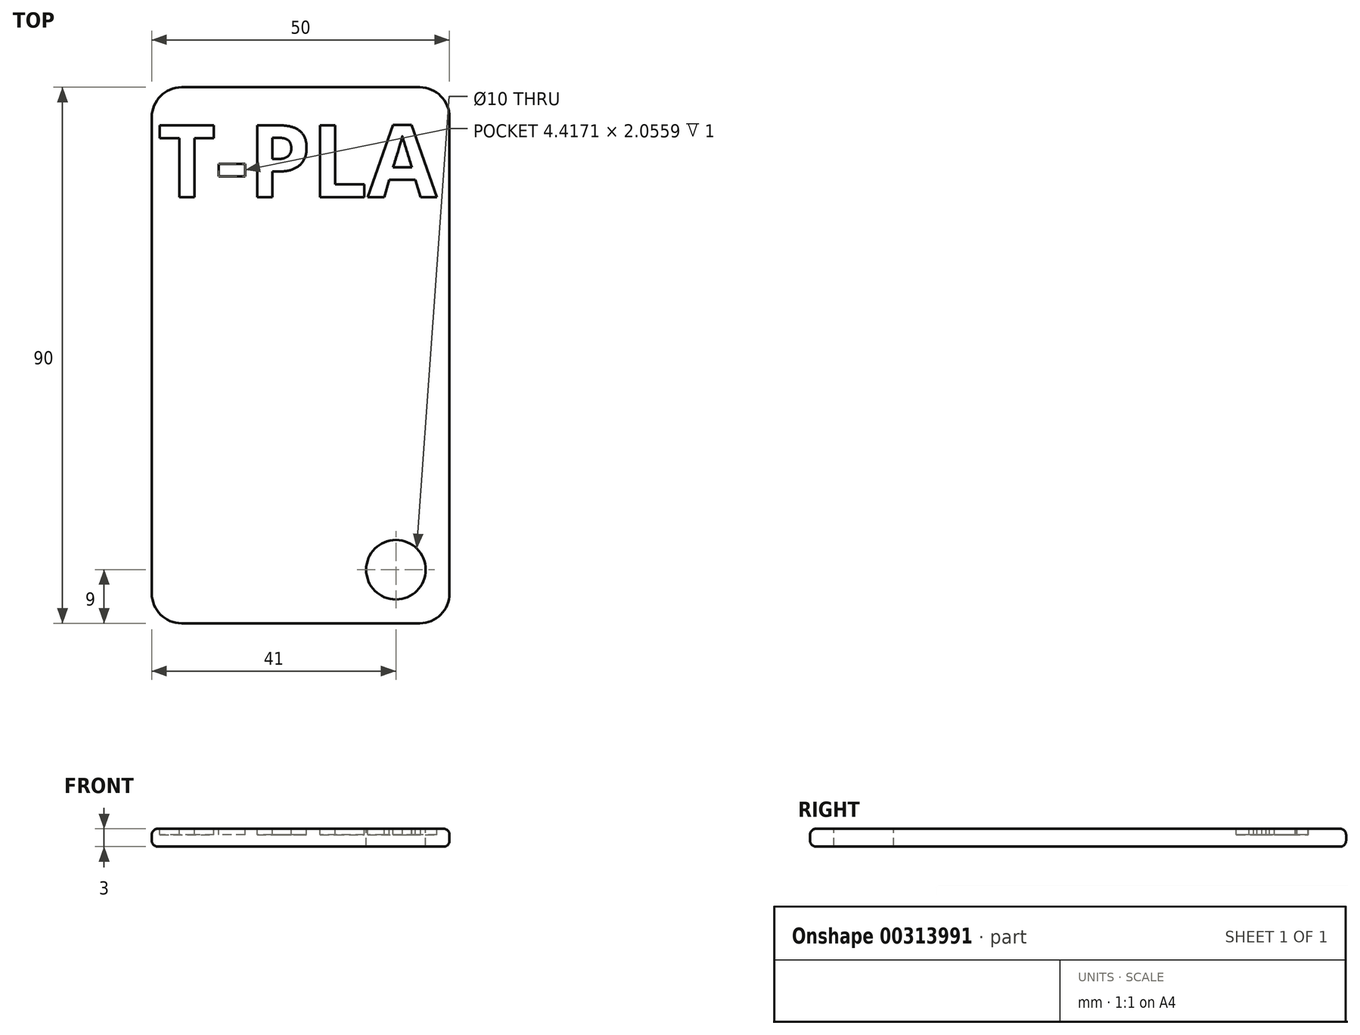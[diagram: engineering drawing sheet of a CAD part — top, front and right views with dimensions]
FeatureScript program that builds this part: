
annotation { "Feature Type Name" : "Feature", "Feature Type Description" : "" }
export const myFeature = defineFeature(function(context is Context, id is Id, definition is map)
    precondition{}
    {
        {
            var Q0;
            Q0=qCreatedBy(makeId("Top.planeOp"),FACE);
            var sketch = newSketch(context, id + "F0", { "sketchPlane" : qUnion([Q0])});
            skLineSegment(sketch, "E0.bottom", {"start": v(-45, 25) * mm, "end": v(45, 25) * mm});
            skLineSegment(sketch, "E0.top", {"start": v(-45, -25) * mm, "end": v(45, -25) * mm});
            skLineSegment(sketch, "E0.left", {"start": v(-45, 25) * mm, "end": v(-45, -25) * mm});
            skLineSegment(sketch, "E0.right", {"start": v(45, 25) * mm, "end": v(45, -25) * mm});
            skLineSegment(sketch, "E1", {"start": v(-45, 25) * mm, "end": v(45, -25) * mm, "construction": true});
            skSolve(sketch);
        }
        {
            var Q0;
            Q0=makeQuery(id+"F0.imprint","IMPRINT",FACE,{"disambiguationData":[TD([[makeQuery(id+"F0.imprint","IMPRINT",EDGE,{"derivedFrom":sQuery(id+"F0.wireOp",EDGE,"E0.bottom")}),-1.0]])]});
            extrude(context, id + "F1", {"entities" : qUnion([Q0]), "depth" : 3 * mm});
        }
        {
            var Q0;
            Q0=makeQuery(id+"F1.opExtrude","CAP_FACE",FACE,{"disambiguationData":[OSD([sQuery(id+"F0.wireOp",EDGE,"E0.bottom"),sQuery(id+"F0.wireOp",EDGE,"E0.top"),sQuery(id+"F0.wireOp",EDGE,"E0.left"),sQuery(id+"F0.wireOp",EDGE,"E0.right")])],"isStart":false});
            var Q1;
            Q1=makeQuery(id+"F1.opExtrude","CAP_FACE",FACE,{"disambiguationData":[OSD([sQuery(id+"F0.wireOp",EDGE,"E0.bottom"),sQuery(id+"F0.wireOp",EDGE,"E0.top"),sQuery(id+"F0.wireOp",EDGE,"E0.left"),sQuery(id+"F0.wireOp",EDGE,"E0.right")])],"isStart":true});
            fillet(context, id + "F2", {"entities" : qUnion([Q0, Q1]), "radius" : 1 * mm, "tangentPropagation" : true, "allowEdgeOverflow" : false});
        }
        {
            var Q0;
            Q0=makeQuery(id+"F1.opExtrude","SWEPT_EDGE",EDGE,{"disambiguationData":[OSD([sQuery(id+"F0.wireOp",EDGE,"E0.top"),sQuery(id+"F0.wireOp",EDGE,"E0.right")])]});
            var Q1;
            Q1=makeQuery(id+"F1.opExtrude","SWEPT_EDGE",EDGE,{"disambiguationData":[OSD([sQuery(id+"F0.wireOp",EDGE,"E0.bottom"),sQuery(id+"F0.wireOp",EDGE,"E0.right")])]});
            var Q2;
            Q2=makeQuery(id+"F1.opExtrude","SWEPT_EDGE",EDGE,{"disambiguationData":[OSD([sQuery(id+"F0.wireOp",EDGE,"E0.bottom"),sQuery(id+"F0.wireOp",EDGE,"E0.left")])]});
            var Q3;
            Q3=makeQuery(id+"F1.opExtrude","SWEPT_EDGE",EDGE,{"disambiguationData":[OSD([sQuery(id+"F0.wireOp",EDGE,"E0.top"),sQuery(id+"F0.wireOp",EDGE,"E0.left")])]});
            fillet(context, id + "F3", {"entities" : qUnion([Q0, Q1, Q2, Q3]), "radius" : 5 * mm, "tangentPropagation" : true, "allowEdgeOverflow" : false});
        }
        {
            var Q0;
            Q0=qCreatedBy(makeId("Right.planeOp"),FACE);
            var sketch = newSketch(context, id + "F4", { "sketchPlane" : qUnion([Q0])});
            skLineSegment(sketch, "E2", {"start": v(0, 0) * mm, "end": v(0, 32.9) * mm});
            skSolve(sketch);
        }
        {
            var Q0;
            Q0=makeQuery(id+"F1.opExtrude","SWEPT_BODY",BODY,{"disambiguationData":[OSD([sQuery(id+"F0.wireOp",EDGE,"E0.bottom"),sQuery(id+"F0.wireOp",EDGE,"E0.top"),sQuery(id+"F0.wireOp",EDGE,"E0.left"),sQuery(id+"F0.wireOp",EDGE,"E0.right")])]});
            var Q1;
            Q1=sQuery(id+"F4.wireOp",EDGE,"E2");
            transform(context, id + "F5", {"entities" : qUnion([Q0]), "transformType" : TransformType.ROTATION, "transformAxis" : qUnion([Q1]), "angle" : 90 * degree, "makeCopy" : false});
        }
        {
            var Q0;
            Q0=makeQuery(id+"F1.opExtrude","CAP_FACE",FACE,{"disambiguationData":[OSD([sQuery(id+"F0.wireOp",EDGE,"E0.bottom"),sQuery(id+"F0.wireOp",EDGE,"E0.top"),sQuery(id+"F0.wireOp",EDGE,"E0.left"),sQuery(id+"F0.wireOp",EDGE,"E0.right")])],"isStart":false});
            var sketch = newSketch(context, id + "F6", { "sketchPlane" : qUnion([Q0])});
            skText(sketch, "E3", { "text": "T-PLA", "fontName": "OpenSans-Bold.ttf"});
            const initialGuessF6  = {"E3": [-0.024, 0.02658, 1, 0, 0.01213]};
            skSetInitialGuess(sketch, initialGuessF6);
            skSolve(sketch);
        }
        {
            var Q0;
            Q0=qSketchRegion(id+"F6",true);
            extrude(context, id + "F7", {"entities" : qUnion([Q0]), "operationType" : NewBodyOperationType.REMOVE, "oppositeDirection" : true, "depth" : 1 * mm});
        }
        {
            var Q0;
            {var subQ0=sQuery(id+"F0.wireOp",EDGE,"E0.left");var subQ2=sQuery(id+"F0.wireOp",EDGE,"E0.bottom");var subQ4=sQuery(id+"F0.wireOp",EDGE,"E0.right");var subQ6=sQuery(id+"F0.wireOp",EDGE,"E0.top");Q0=makeQuery(id+"F7.boolean.opBoolean","SPLIT",FACE,{"disambiguationData":[TD([makeQuery(id+"F7.opExtrude","SWEPT_FACE",FACE,{"disambiguationData":[OSD([sQuery(id+"F6.wireOp",EDGE,"E3.sketch_text.stroke-0")])]})])],"derivedFrom":makeQuery(id+"F1.opExtrude","CAP_FACE",FACE,{"disambiguationData":[OSD([subQ2,subQ6,subQ0,subQ4])],"isStart":false})});}
            var sketch = newSketch(context, id + "F8", { "sketchPlane" : qUnion([Q0])});
            skCircle(sketch, "E4", {"center": v(16, -36) * mm, "radius": 5 * mm});
            skSolve(sketch);
        }
        {
            var Q0;
            Q0=qSketchRegion(id+"F8",true);
            extrude(context, id + "F9", {"entities" : qUnion([Q0]), "operationType" : NewBodyOperationType.REMOVE, "oppositeDirection" : true, "depth" : 3 * mm});
        }
    });
